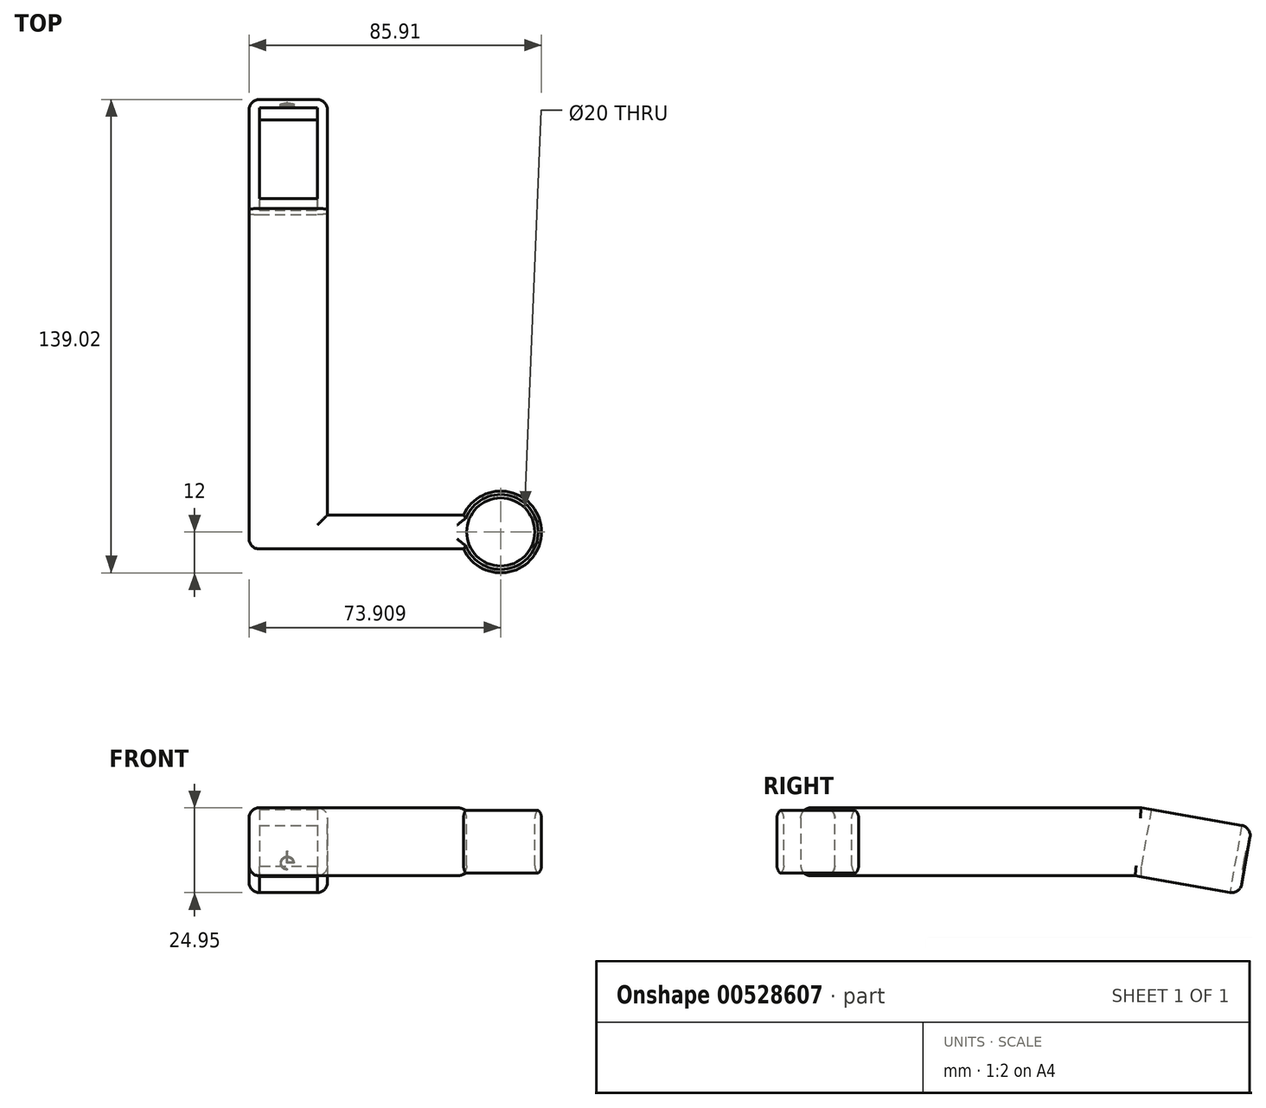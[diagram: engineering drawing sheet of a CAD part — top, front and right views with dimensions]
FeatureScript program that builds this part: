
annotation { "Feature Type Name" : "Feature", "Feature Type Description" : "" }
export const myFeature = defineFeature(function(context is Context, id is Id, definition is map)
    precondition{}
    {
        {
            var Q0;
            Q0=qCreatedBy(makeId("Top.planeOp"),FACE);
            var sketch = newSketch(context, id + "F0", { "sketchPlane" : qUnion([Q0])});
            skLineSegment(sketch, "E0.bottom", {"start": v(0, 0) * mm, "end": v(17, 0) * mm});
            skLineSegment(sketch, "E0.top", {"start": v(0, 27) * mm, "end": v(17, 27) * mm});
            skLineSegment(sketch, "E0.left", {"start": v(0, 0) * mm, "end": v(0, 27) * mm});
            skLineSegment(sketch, "E0.right", {"start": v(17, 0) * mm, "end": v(17, 27) * mm});
            skLineSegment(sketch, "E1.0", {"start": v(20, -3) * mm, "end": v(20, 30) * mm});
            skLineSegment(sketch, "E1.1", {"start": v(-3, -3) * mm, "end": v(20, -3) * mm});
            skLineSegment(sketch, "E1.2", {"start": v(-3, -3) * mm, "end": v(-3, 30) * mm});
            skLineSegment(sketch, "E1.3", {"start": v(-3, 30) * mm, "end": v(20, 30) * mm});
            skSolve(sketch);
        }
        {
            var Q0;
            Q0=makeQuery(id+"F0.imprint","IMPRINT",FACE,{"disambiguationData":[TD([[makeQuery(id+"F0.imprint","IMPRINT",EDGE,{"derivedFrom":sQuery(id+"F0.wireOp",EDGE,"E0.bottom")}),-1.0]])]});
            extrude(context, id + "F1", {"entities" : qUnion([Q0]), "depth" : 20 * mm});
        }
        {
            var Q0;
            Q0=makeQuery(id+"F1.opExtrude","SWEPT_FACE",FACE,{"disambiguationData":[OSD([sQuery(id+"F0.wireOp",EDGE,"E1.0")])]});
            var sketch = newSketch(context, id + "F2", { "sketchPlane" : qUnion([Q0])});
            skLineSegment(sketch, "E2.bottom", {"start": v(-3, 0) * mm, "end": v(-93, 0) * mm});
            skLineSegment(sketch, "E2.top", {"start": v(-3, 20) * mm, "end": v(-93, 20) * mm});
            skLineSegment(sketch, "E2.left", {"start": v(-3, 0) * mm, "end": v(-3, 20) * mm});
            skLineSegment(sketch, "E2.right", {"start": v(-93, 0) * mm, "end": v(-93, 20) * mm});
            skSolve(sketch);
        }
        {
            var Q0;
            Q0=makeQuery(id+"F1.opExtrude","SWEPT_BODY",BODY,{"disambiguationData":[OSD([sQuery(id+"F0.wireOp",EDGE,"E0.bottom"),sQuery(id+"F0.wireOp",EDGE,"E0.top"),sQuery(id+"F0.wireOp",EDGE,"E0.left"),sQuery(id+"F0.wireOp",EDGE,"E0.right"),sQuery(id+"F0.wireOp",EDGE,"E1.0"),sQuery(id+"F0.wireOp",EDGE,"E1.1"),sQuery(id+"F0.wireOp",EDGE,"E1.2"),sQuery(id+"F0.wireOp",EDGE,"E1.3")])]});
            var Q1;
            Q1=makeQuery(id+"F1.opExtrude","CAP_EDGE",EDGE,{"disambiguationData":[OSD([sQuery(id+"F0.wireOp",EDGE,"E1.1")])],"isStart":false});
            transform(context, id + "F3", {"entities" : qUnion([Q0]), "transformType" : TransformType.ROTATION, "transformAxis" : qUnion([Q1]), "angle" : 10 * degree, "oppositeDirection" : true, "makeCopy" : false});
        }
        {
            var Q0;
            Q0=makeQuery(id+"F2.imprint","IMPRINT",FACE,{"disambiguationData":[TD([[makeQuery(id+"F2.imprint","IMPRINT",EDGE,{"derivedFrom":sQuery(id+"F2.wireOp",EDGE,"E2.bottom")}),-1.0]])]});
            extrude(context, id + "F4", {"entities" : qUnion([Q0]), "operationType" : NewBodyOperationType.ADD, "oppositeDirection" : true, "depth" : 23 * mm});
        }
        {
            var Q0;
            Q0=makeQuery(id+"F4.boolean.opBoolean","MERGE",FACE,{"derivedFrom":[makeQuery(id+"F1.opExtrude","SWEPT_FACE",FACE,{"disambiguationData":[OSD([sQuery(id+"F0.wireOp",EDGE,"E1.0")])]}),makeQuery(id+"F4.opExtrude","CAP_FACE",FACE,{"disambiguationData":[OSD([sQuery(id+"F2.wireOp",EDGE,"E2.bottom"),sQuery(id+"F2.wireOp",EDGE,"E2.top"),sQuery(id+"F2.wireOp",EDGE,"E2.left"),sQuery(id+"F2.wireOp",EDGE,"E2.right")])],"isStart":true})]});
            var sketch = newSketch(context, id + "F5", { "sketchPlane" : qUnion([Q0])});
            skLineSegment(sketch, "E3.bottom", {"start": v(-93, 20) * mm, "end": v(-103, 20) * mm});
            skLineSegment(sketch, "E3.top", {"start": v(-93, 0) * mm, "end": v(-103, 0) * mm});
            skLineSegment(sketch, "E3.left", {"start": v(-93, 20) * mm, "end": v(-93, 0) * mm});
            skLineSegment(sketch, "E3.right", {"start": v(-103, 20) * mm, "end": v(-103, 0) * mm});
            skSolve(sketch);
        }
        {
            var Q0;
            Q0=makeQuery(id+"F5.imprint","IMPRINT",FACE,{"disambiguationData":[TD([[makeQuery(id+"F5.imprint","IMPRINT",EDGE,{"derivedFrom":sQuery(id+"F5.wireOp",EDGE,"E3.bottom")}),1.0]])]});
            extrude(context, id + "F6", {"entities" : qUnion([Q0]), "operationType" : NewBodyOperationType.ADD, "depth" : 40 * mm, "hasSecondDirection" : true, "secondDirectionOppositeDirection" : true, "secondDirectionDepth" : 23 * mm});
        }
        {
            var Q0;
            Q0=makeQuery(id+"F6.boolean.opBoolean","MERGE",FACE,{"derivedFrom":[makeQuery(id+"F4.opExtrude","SWEPT_FACE",FACE,{"disambiguationData":[OSD([sQuery(id+"F2.wireOp",EDGE,"E2.top")])]}),makeQuery(id+"F6.opExtrude","SWEPT_FACE",FACE,{"disambiguationData":[OSD([sQuery(id+"F5.wireOp",EDGE,"E3.bottom")])]})]});
            var sketch = newSketch(context, id + "F7", { "sketchPlane" : qUnion([Q0])});
            skArc(sketch, "E4", {"start": v(60, -103) * mm, "mid": v(82.9, -98) * mm, "end": v(60, -93) * mm});
            skCircle(sketch, "E5", {"center": v(70.9, -98) * mm, "radius": 10 * mm});
            skSolve(sketch);
        }
        {
            var Q0;
            Q0=makeQuery(id+"F7.imprint","IMPRINT",FACE,{"disambiguationData":[TD([[makeQuery(id+"F7.imprint","IMPRINT",EDGE,{"derivedFrom":sQuery(id+"F7.wireOp",EDGE,"E4")}),1.0]])]});
            extrude(context, id + "F8", {"entities" : qUnion([Q0]), "operationType" : NewBodyOperationType.ADD, "oppositeDirection" : true, "depth" : 20 * mm});
        }
        {
            var Q0;
            Q0=makeQuery(id+"F8.opExtrude","CAP_EDGE",EDGE,{"disambiguationData":[OSD([sQuery(id+"F7.wireOp",EDGE,"E5")])],"isStart":false});
            var Q1;
            Q1=makeQuery(id+"F8.opExtrude","CAP_EDGE",EDGE,{"disambiguationData":[OSD([sQuery(id+"F7.wireOp",EDGE,"E5")])],"isStart":true});
            var Q2;
            Q2=makeQuery(id+"F6.opExtrude","SWEPT_EDGE",EDGE,{"disambiguationData":[OSD([sQuery(id+"F2.wireOp",EDGE,"E2.top"),sQuery(id+"F5.wireOp",EDGE,"E3.bottom"),sQuery(id+"F5.wireOp",EDGE,"E3.left")])]});
            var Q3;
            Q3=makeQuery(id+"F6.opExtrude","SWEPT_EDGE",EDGE,{"disambiguationData":[OSD([sQuery(id+"F5.wireOp",EDGE,"E3.bottom"),sQuery(id+"F5.wireOp",EDGE,"E3.right")])]});
            var Q4;
            Q4=makeQuery(id+"F8.opExtrude","CAP_EDGE",EDGE,{"disambiguationData":[OSD([sQuery(id+"F7.wireOp",EDGE,"E4")])],"isStart":true});
            var Q5;
            Q5=makeQuery(id+"F8.opExtrude","CAP_EDGE",EDGE,{"disambiguationData":[OSD([sQuery(id+"F7.wireOp",EDGE,"E4")])],"isStart":false});
            var Q6;
            Q6=makeQuery(id+"F6.opExtrude","SWEPT_EDGE",EDGE,{"disambiguationData":[OSD([sQuery(id+"F2.wireOp",EDGE,"E2.bottom"),sQuery(id+"F5.wireOp",EDGE,"E3.top"),sQuery(id+"F5.wireOp",EDGE,"E3.left")])]});
            var Q7;
            Q7=makeQuery(id+"F6.opExtrude","SWEPT_EDGE",EDGE,{"disambiguationData":[OSD([sQuery(id+"F5.wireOp",EDGE,"E3.top"),sQuery(id+"F5.wireOp",EDGE,"E3.right")])]});
            var Q8;
            Q8=makeQuery(id+"F4.opExtrude","CAP_EDGE",EDGE,{"disambiguationData":[OSD([sQuery(id+"F2.wireOp",EDGE,"E2.top")])],"isStart":true});
            var Q9;
            Q9=makeQuery(id+"F6.boolean.opBoolean","MERGE",EDGE,{"derivedFrom":[makeQuery(id+"F4.opExtrude","CAP_EDGE",EDGE,{"disambiguationData":[OSD([sQuery(id+"F2.wireOp",EDGE,"E2.top")])],"isStart":false}),makeQuery(id+"F6.opExtrude","CAP_EDGE",EDGE,{"disambiguationData":[OSD([sQuery(id+"F5.wireOp",EDGE,"E3.bottom")])],"isStart":true})]});
            var Q10;
            Q10=makeQuery(id+"F6.boolean.opBoolean","MERGE",EDGE,{"derivedFrom":[makeQuery(id+"F4.opExtrude","CAP_EDGE",EDGE,{"disambiguationData":[OSD([sQuery(id+"F2.wireOp",EDGE,"E2.bottom")])],"isStart":false}),makeQuery(id+"F6.opExtrude","CAP_EDGE",EDGE,{"disambiguationData":[OSD([sQuery(id+"F5.wireOp",EDGE,"E3.top")])],"isStart":true})]});
            var Q11;
            Q11=makeQuery(id+"F4.opExtrude","CAP_EDGE",EDGE,{"disambiguationData":[OSD([sQuery(id+"F2.wireOp",EDGE,"E2.bottom")])],"isStart":true});
            var Q12;
            Q12=makeQuery(id+"F1.opExtrude","CAP_EDGE",EDGE,{"disambiguationData":[OSD([sQuery(id+"F0.wireOp",EDGE,"E1.0")])],"isStart":true});
            var Q13;
            Q13=makeQuery(id+"F1.opExtrude","CAP_EDGE",EDGE,{"disambiguationData":[OSD([sQuery(id+"F0.wireOp",EDGE,"E1.3")])],"isStart":true});
            var Q14;
            Q14=makeQuery(id+"F1.opExtrude","CAP_EDGE",EDGE,{"disambiguationData":[OSD([sQuery(id+"F0.wireOp",EDGE,"E1.2")])],"isStart":true});
            var Q15;
            Q15=makeQuery(id+"F1.opExtrude","CAP_EDGE",EDGE,{"disambiguationData":[OSD([sQuery(id+"F0.wireOp",EDGE,"E1.0")])],"isStart":false});
            var Q16;
            Q16=makeQuery(id+"F1.opExtrude","CAP_EDGE",EDGE,{"disambiguationData":[OSD([sQuery(id+"F0.wireOp",EDGE,"E1.2")])],"isStart":false});
            var Q17;
            Q17=makeQuery(id+"F1.opExtrude","SWEPT_EDGE",EDGE,{"disambiguationData":[OSD([sQuery(id+"F0.wireOp",EDGE,"E1.2"),sQuery(id+"F0.wireOp",EDGE,"E1.3")])]});
            var Q18;
            Q18=makeQuery(id+"F1.opExtrude","SWEPT_EDGE",EDGE,{"disambiguationData":[OSD([sQuery(id+"F0.wireOp",EDGE,"E1.0"),sQuery(id+"F0.wireOp",EDGE,"E1.3")])]});
            var Q19;
            Q19=makeQuery(id+"F1.opExtrude","CAP_EDGE",EDGE,{"disambiguationData":[OSD([sQuery(id+"F0.wireOp",EDGE,"E1.3")])],"isStart":false});
            var Q20;
            Q20=makeQuery(id+"F6.opExtrude","CAP_EDGE",EDGE,{"disambiguationData":[OSD([sQuery(id+"F5.wireOp",EDGE,"E3.right")])],"isStart":true});
            var Q21;
            Q21=makeQuery(id+"F4.opExtrude","CAP_EDGE",EDGE,{"disambiguationData":[OSD([sQuery(id+"F2.wireOp",EDGE,"E2.right")])],"isStart":true});
            fillet(context, id + "F9", {"entities" : qUnion([Q0, Q1, Q2, Q3, Q4, Q5, Q6, Q7, Q8, Q9, Q10, Q11, Q12, Q13, Q14, Q15, Q16, Q17, Q18, Q19, Q20, Q21]), "radius" : 3 * mm, "tangentPropagation" : true, "allowEdgeOverflow" : false});
        }
        {
            var Q0;
            Q0=makeQuery(id+"F1.opExtrude","SWEPT_FACE",FACE,{"disambiguationData":[OSD([sQuery(id+"F0.wireOp",EDGE,"E1.3")])]});
            var sketch = newSketch(context, id + "F10", { "sketchPlane" : qUnion([Q0])});
            skLineSegment(sketch, "E6.bottom", {"start": v(-8.2, 6.44) * mm, "end": v(-10.2, 6.44) * mm, "construction": true});
            skLineSegment(sketch, "E6.top", {"start": v(-8.2, 8.44) * mm, "end": v(-10.2, 8.44) * mm, "construction": true});
            skLineSegment(sketch, "E6.left", {"start": v(-8.2, 6.44) * mm, "end": v(-8.2, 8.44) * mm, "construction": true});
            skLineSegment(sketch, "E6.right", {"start": v(-10.2, 6.44) * mm, "end": v(-10.2, 8.44) * mm, "construction": true});
            skArc(sketch, "E7", {"start": v(-8.2, 6.44) * mm, "mid": v(-6.79, 9.85) * mm, "end": v(-10.2, 8.44) * mm});
            skLineSegment(sketch, "E8", {"start": v(-8.2, 6.44) * mm, "end": v(-8.2, 6.69) * mm});
            skLineSegment(sketch, "E9", {"start": v(-10.2, 8.44) * mm, "end": v(-9.95, 8.44) * mm});
            skArc(sketch, "E10", {"start": v(-8.2, 6.69) * mm, "mid": v(-6.96, 9.67) * mm, "end": v(-9.95, 8.44) * mm});
            skLineSegment(sketch, "E11", {"start": v(-9.95, 8.44) * mm, "end": v(-8.08, 8.44) * mm});
            skLineSegment(sketch, "E12", {"start": v(-8.08, 8.44) * mm, "end": v(-8.08, 11.94) * mm});
            skLineSegment(sketch, "E13", {"start": v(-8.08, 11.94) * mm, "end": v(-8.33, 11.94) * mm});
            skLineSegment(sketch, "E14", {"start": v(-9.93, 8.69) * mm, "end": v(-8.33, 8.69) * mm});
            skLineSegment(sketch, "E15", {"start": v(-8.33, 8.69) * mm, "end": v(-8.33, 11.94) * mm});
            skSolve(sketch);
        }
        {
            var Q0;
            {var subQ1=sQuery(id+"F10.wireOp",EDGE,"E11");Q0=makeQuery(id+"F10.imprint","IMPRINT",FACE,{"disambiguationData":[TD([[makeQuery(id+"F10.imprint","IMPRINT",EDGE,{"derivedFrom":subQ1}),1.0]])]});}
            var Q1;
            {var subQ0=sQuery(id+"F10.wireOp",EDGE,"E8");Q1=makeQuery(id+"F10.imprint","IMPRINT",FACE,{"disambiguationData":[TD([[makeQuery(id+"F10.imprint","IMPRINT",EDGE,{"derivedFrom":subQ0}),-1.0]])]});}
            var Q2;
            {var subQ5=sQuery(id+"F10.wireOp",EDGE,"E13");Q2=makeQuery(id+"F10.imprint","IMPRINT",FACE,{"disambiguationData":[TD([[makeQuery(id+"F10.imprint","IMPRINT",EDGE,{"derivedFrom":subQ5}),1.0]])]});}
            var Q3;
            {var subQ0=sQuery(id+"F10.wireOp",EDGE,"E12");var subQ1=sQuery(id+"F10.wireOp",EDGE,"E7");var subQ2=makeQuery(id+"F10.imprint","INTERSECT",VERTEX,{"derivedFrom":[subQ1,subQ0]});Q3=makeQuery(id+"F10.imprint","IMPRINT",FACE,{"disambiguationData":[TD([[makeQuery(id+"F10.imprint","IMPRINT",EDGE,{"disambiguationData":[TD([[subQ2,-1.0]])],"derivedFrom":subQ1}),1.0]])]});}
            var Q4;
            {var subQ1=sQuery(id+"F10.wireOp",EDGE,"E9");Q4=makeQuery(id+"F10.imprint","IMPRINT",FACE,{"disambiguationData":[TD([[makeQuery(id+"F10.imprint","IMPRINT",EDGE,{"derivedFrom":subQ1}),1.0]])]});}
            extrude(context, id + "F11", {"entities" : qUnion([Q0, Q1, Q2, Q3, Q4]), "operationType" : NewBodyOperationType.REMOVE, "oppositeDirection" : true, "depth" : .5 * mm, "offsetDistance" : 25 * mm});
        }
    });
